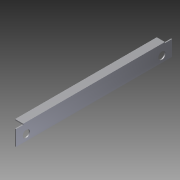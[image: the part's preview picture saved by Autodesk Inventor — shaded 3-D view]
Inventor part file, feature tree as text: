
AUTODESK INVENTOR PART (.ipt)
format: ipt  version: 2012 (Build 160160000, 160)  size: 99,328 bytes
history: native  units: in
note: dims shown in document units (in); Inventor stores cm internally (conversion verified against a paired STEP export)
features: extrude x3, sketch x3
ambient origin geometry x8: Origin, YZ Plane, XZ Plane, XY Plane, X Axis, Y Axis, Z Axis, Center Point
bodies: Solid1 (feature_tree)
feature tree (6):
  extrude  "Extrusion1"  Depth=1.0in
  extrude  "Extrusion2"  Depth=0.125in
  extrude  "Extrusion3"  Depth=0.875in
  sketch  "Sketch1"  dims[d0=2.0in d1=1.0in]
  sketch  "Sketch2"  dims[d2=0.125in d3=0.125in]
  sketch  "Sketch3"  dims[d4=19.0in d5=0.0in d6=0.875in d7=1.25in d8=1.25in d11=20.0in d12=0.0in d13=0.875in d14=0.125in d15=0.0in d16=0.875in d17=1.25in d18=1.25in]
